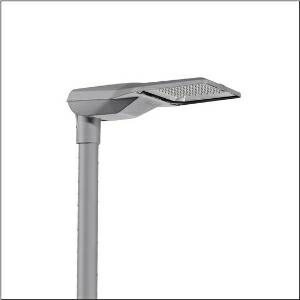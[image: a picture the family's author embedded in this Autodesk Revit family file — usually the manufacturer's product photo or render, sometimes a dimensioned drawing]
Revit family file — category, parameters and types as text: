
# Revit family: streetlight_sl_21_iq_midi___st0_8a_5xe3c31g08nb_0abe
name_source: partatom
category: Lighting Fixtures
units: mm (PartAtom-declared; Revit-internal decimal feet)

## family parameters
Cut with Voids When Loaded = No
Host = Face
Light Source = No
Part Type = Normal
Room Calculation Point = No
Round Connector Dimension = Use Diameter
Shared = No

## types (1)
- --- (1 x LED, 23230 lm, 155.5 W, 3000K)
    Apparent Load = 155 VA
    CIE Flux Codes = 41 75 97 100 100
    Color Rendering = 70
    Color Temperature = 3000K
    Default Elevation = 1800 mm
    Description = Streetlight SL 21 iQ midi, mast luminaire, primary light control with lens, of PMMA, primary optical cover: cover, of toughened safety glass, transparent, light distribution: ST0.8a, light emission: direct distribution, primary light characteristic: asymmetric, installation type: post-top, side-entry, LED, High Power LED, rated luminous flux: 23.230lm, luminous efficacy: 149lm/W, light colour: 730, colour temperature: 3000K, control gear: iQ Street-Remote, control: Street-Remote, Auto-Match, Temp-Guard, Lumen-Switch, Night-Set, Smart-Wire, Light-Fading, Desk-Remote (wireless, voltage-free reading and setting of iQ features in the workshop via application-optimized NFC function/RFID function), optimised constant luminous flux control (CLO 2.0), pre-setting: linear dimming characteristic, mains connection: 230..240V, AC, 50/60Hz, start of lifetime: 156W, end of service life: 162W, reduction: 69W, luminaire housing, of diecast aluminium, powder-coated, Siteco® metallic grey (DB 702S), corrosivity category C5 mid according to DIN EN ISO 12944, please order mast flange separately, inclination adjustable: 0°, 5°, 10°, 15°, sealing non-destructively replaceable, multi-level sealing system, length: 644mm, width: 335mm, height: 110mm, mast flange for spigot size: 42mm (side-entry): 5XC10008XM4, 60/48mm (side-entry/post-top): 5XC10108XM2, 76/60mm (side-entry/post-top): 5XC10108XM1, mounting height: 4..8m, protection rating (complete): IP66, insulation class (complete): insulation class II (safety insulation), certification: CE, ENEC, ENEC+, VDE, impact resistance: IK10, permissible operating ambient temperature for outdoor applications: -40..+50°C, standard-compliant lighting for roads and squares, packaging unit: 1 piece

Light Distribution: ST0.8a
    Height = 111 mm
    Lamp = 1 x LED
    Lamp Light Flux = 23230 lm
    Lamp Power = 155.5 W
    Lamp count = 1
    Length = 644 mm
    Luminous efficacy = 149 lm/W
    Manufacturer = Siteco
    ModVariant = No
    Model = 5XE3C31G08NB
    Number of Poles = 1
    OnlyDefault = Yes
    Power Factor = 1
    Product Name = Streetlight SL 21 iQ midi | ST0.8a
    Product group = mast luminaire | pylon top
    ProductGroupID = 6100
    Protection Class = Protection class II
    Protection Degree = IP 66
    RLX_Detail_Level = 1
    RLX_Emergency_Light_Flux = 0 lm
    RLX_Emergency_Type = 0
    RLX_Emergency_Type_DB = No
    RlxData = <blob elided: 27237 chars, md5=4311b7c4>
    Socket = socket
    Standby Power = 0 W
    System Light Flux = 23230 lm
    System Power = 155 W
    Type Comments = factory setting: luminous flux: 100 % | dim-lin: 254 | 823 mA
    Type Image = l_1004298.jpg
    URL = http://relux.com
    VarID = @adj_190421
    Voltage = 0 V
    Weight = 0.00 kg
    Width = 336 mm

## geometry (parser evidence)
native form markers: Blend x4, Sweep x11
no freeform markers — native parametric forms only
